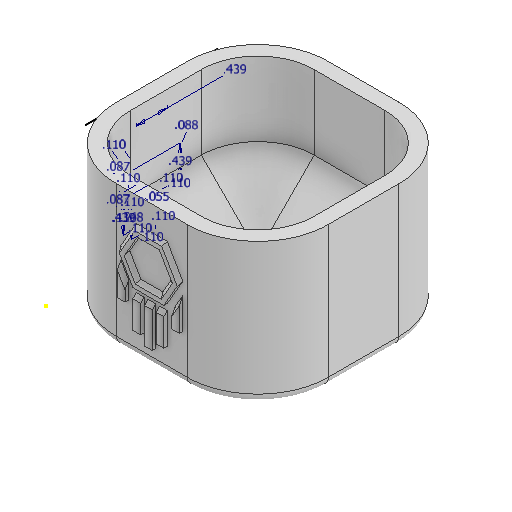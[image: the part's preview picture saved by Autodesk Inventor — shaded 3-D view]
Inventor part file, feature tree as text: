
AUTODESK INVENTOR PART (.ipt)
format: ipt  version: 2025.1 (Build 291241020, 241B)  size: 309,760 bytes
history: native  units: in
note: dims shown in document units (in); Inventor stores cm internally (conversion verified against a paired STEP export)
features: sketch x6, extrude x5, fillet x2, chamfer x2, projected_geometry x1
ambient origin geometry x8: Origin, YZ Plane, XZ Plane, XY Plane, X Axis, Y Axis, Z Axis, Center Point
bodies: Solid1 (feature_tree)
feature tree (16):
  extrude  "Extrusion1"  Depth=3.0in
  extrude  "Extrusion3"  Depth=1.26in
  extrude  "Extrusion4"  Depth=1.0in
  fillet  "Fillet1"  Radius=0.16in
  extrude  "Extrusion5"  Depth=0.86in
  fillet  "Fillet2"  Radius=0.46in
  chamfer  "Chamfer1"  Distance=0.5in
  sketch  "Sketch6"  dims[d20=1.0in d21=0.2in d22=1.8in d23=0.0in]
  extrude  "Extrusion6"  Depth=0.2in
  chamfer  "Chamfer2"  Distance=1.8in
  sketch  "Sketch1"  dims[d0=3.0in d1=3.0in]
  sketch  "Sketch3"  dims[d2=2.0in d3=0.0in d10=1.26in]
  sketch  "Sketch4"  dims[d11=0.48in d12=1.0in d13=0.16in]
  sketch  "Sketch5"  dims[d14=0.25in d15=0.0in d16=0.86in d17=0.46in d18=0.5in d19=0.0in]
  projected_geometry  "Projected Loop1"
  sketch  "Sketch7"  dims[d24=0.125in d25=0.75in d26=0.125in d27=45.0deg d28=0.439in d29=0.1099in d30=0.0873in d31=0.0875in d32=0.1097in d33=0.1097in d34=0.1097in d35=0.1097in d36=0.0873in d37=0.4387in d38=0.4387in d39=0.5484in d40=0.1097in d41=0.1097in d42=0.1097in d43=0.0548in d44=0.1099in d45=0.439in d46=0.1099in d47=0.0873in d48=0.0875in d49=0.1097in d50=0.1097in d51=0.1097in d52=0.1097in d53=0.0873in d54=0.4387in d55=0.4387in d56=0.5484in d57=0.1097in d58=0.1097in d59=0.1097in d60=0.0548in d61=0.1099in d62=0.05in d63=0.0in d64=0.05in d65=0.125in d66=45.0deg]
